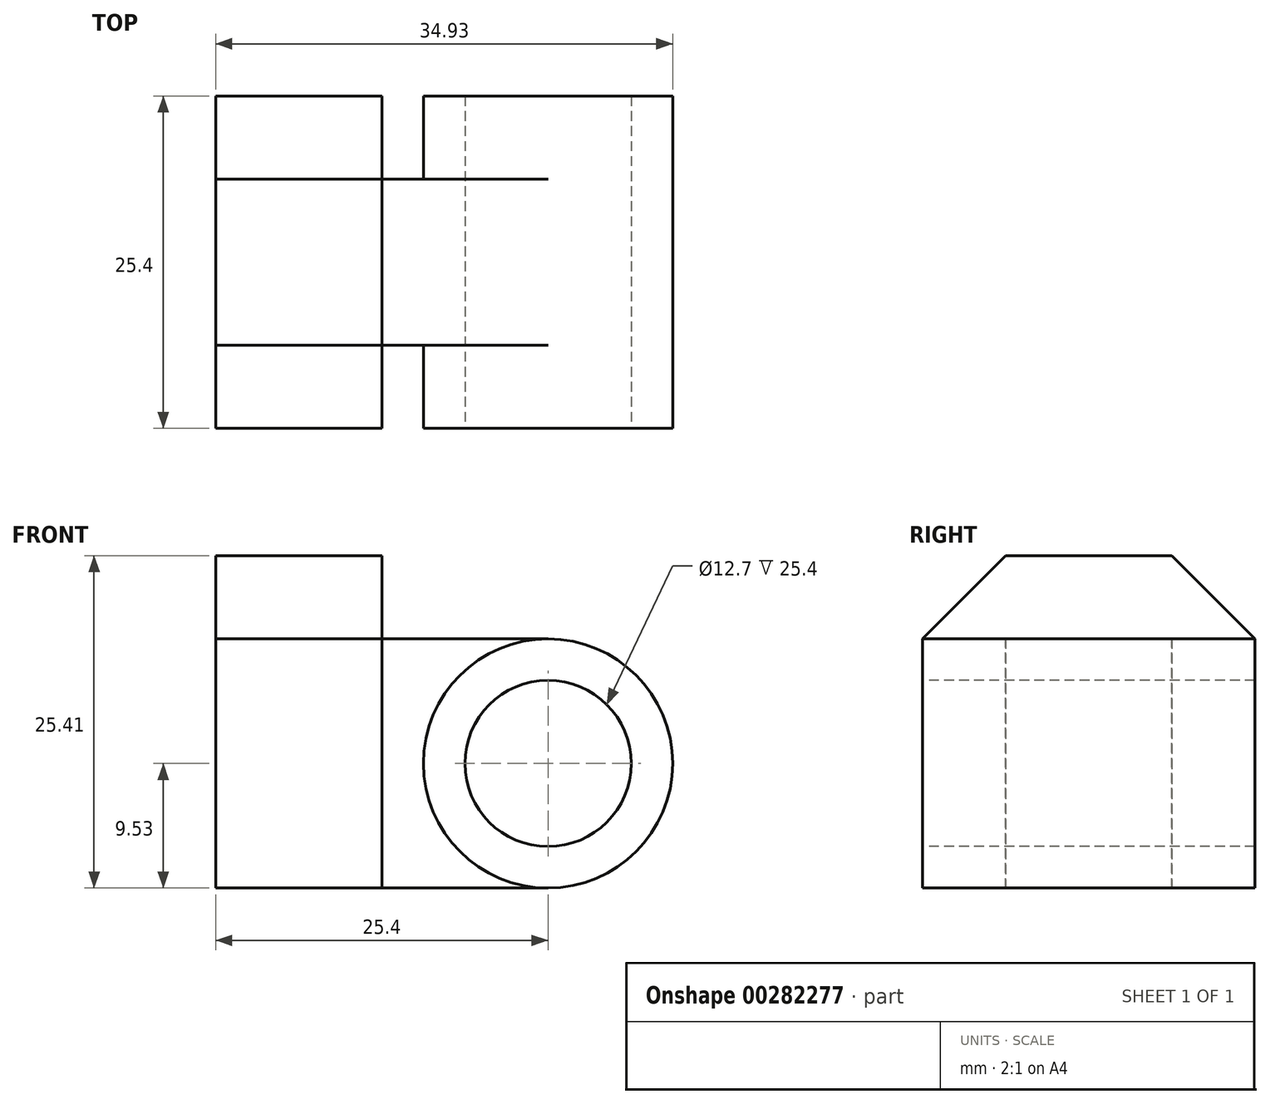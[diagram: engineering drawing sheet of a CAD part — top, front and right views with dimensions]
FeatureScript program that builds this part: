
annotation { "Feature Type Name" : "Feature", "Feature Type Description" : "" }
export const myFeature = defineFeature(function(context is Context, id is Id, definition is map)
    precondition{}
    {
        {
            var Q0;
            Q0=qCreatedBy(makeId("Front.planeOp"),FACE);
            var sketch = newSketch(context, id + "F0", { "sketchPlane" : qUnion([Q0])});
            skCircle(sketch, "E0", {"center": v(0, 0) * mm, "radius": 9.53 * mm});
            skSolve(sketch);
        }
        {
            var Q0;
            Q0 = qSketchRegion(id + "F0", true);
            extrude(context, id + "F1", {"entities" : qUnion([Q0]), "oppositeDirection" : true, "depth" : 25.4 * mm});
        }
        {
            var Q0;
            Q0=qCreatedBy(makeId("Front.planeOp"),FACE);
            var sketch = newSketch(context, id + "F2", { "sketchPlane" : qUnion([Q0])});
            skCircle(sketch, "E1", {"center": v(0, 0) * mm, "radius": 6.35 * mm});
            skSolve(sketch);
        }
        {
            var Q0;
            Q0 = qSketchRegion(id + "F2", true);
            extrude(context, id + "F3", {"entities" : qUnion([Q0]), "operationType" : NewBodyOperationType.REMOVE, "oppositeDirection" : true, "depth" : 25.4 * mm});
        }
        {
            var Q0;
            Q0=qCreatedBy(makeId("Front.planeOp"),FACE);
            cPlane(context, id + "F4", {"entities" : qUnion([Q0]), "cplaneType" : CPlaneType.OFFSET, "offset" : 12.7 * mm, "oppositeDirection" : true, "width" : 152.4 * mm, "height" : 152.4 * mm});
        }
        {
            var Q0;
            Q0=qCreatedBy(id+"F4.planeOp",FACE);
            var sketch = newSketch(context, id + "F5", { "sketchPlane" : qUnion([Q0])});
            skLineSegment(sketch, "E2", {"start": v(0, -9.53) * mm, "end": v(-12.7, -9.53) * mm});
            skLineSegment(sketch, "E3", {"start": v(-12.7, -9.53) * mm, "end": v(-12.7, 9.53) * mm});
            skLineSegment(sketch, "E4", {"start": v(-12.7, 9.53) * mm, "end": v(0, 9.53) * mm});
            skArc(sketch, "E5", {"start": v(0, 9.53) * mm, "mid": v(-9.53, 0) * mm, "end": v(0, -9.53) * mm});
            skSolve(sketch);
        }
        {
            var Q0;
            Q0 = qSketchRegion(id + "F5", true);
            extrude(context, id + "F6", {"entities" : qUnion([Q0]), "operationType" : NewBodyOperationType.ADD, "endBound" : BoundingType.SYMMETRIC, "depth" : 12.7 * mm});
        }
        {
            var Q0;
            Q0=makeQuery(id+"F6.opExtrude","SWEPT_FACE",FACE,{"disambiguationData":[OSD([sQuery(id+"F5.wireOp",EDGE,"E3")])]});
            var sketch = newSketch(context, id + "F7", { "sketchPlane" : qUnion([Q0])});
            skLineSegment(sketch, "E6", {"start": v(0, -9.53) * mm, "end": v(0, 9.53) * mm});
            skPoint(sketch, "E6.startSnap0", {"position": v(-12.7, -9.53) * mm});
            skLineSegment(sketch, "E7", {"start": v(0, 9.52) * mm, "end": v(-6.35, 15.88) * mm});
            skLineSegment(sketch, "E8", {"start": v(-6.35, 15.88) * mm, "end": v(-19.05, 15.88) * mm});
            skLineSegment(sketch, "E9", {"start": v(-19.05, 15.88) * mm, "end": v(-25.4, 9.53) * mm});
            skLineSegment(sketch, "E10", {"start": v(-25.4, 9.53) * mm, "end": v(-25.4, -9.53) * mm});
            skLineSegment(sketch, "E11", {"start": v(-25.4, -9.52) * mm, "end": v(0, -9.52) * mm});
            skLineSegment(sketch, "E12", {"start": v(-12.7, -9.53) * mm, "end": v(-12.7, 15.88) * mm, "construction": true});
            skSolve(sketch);
        }
        {
            var Q0;
            Q0 = qSketchRegion(id + "F7", true);
            extrude(context, id + "F8", {"entities" : qUnion([Q0]), "operationType" : NewBodyOperationType.ADD, "depth" : 12.7 * mm});
        }
    });
